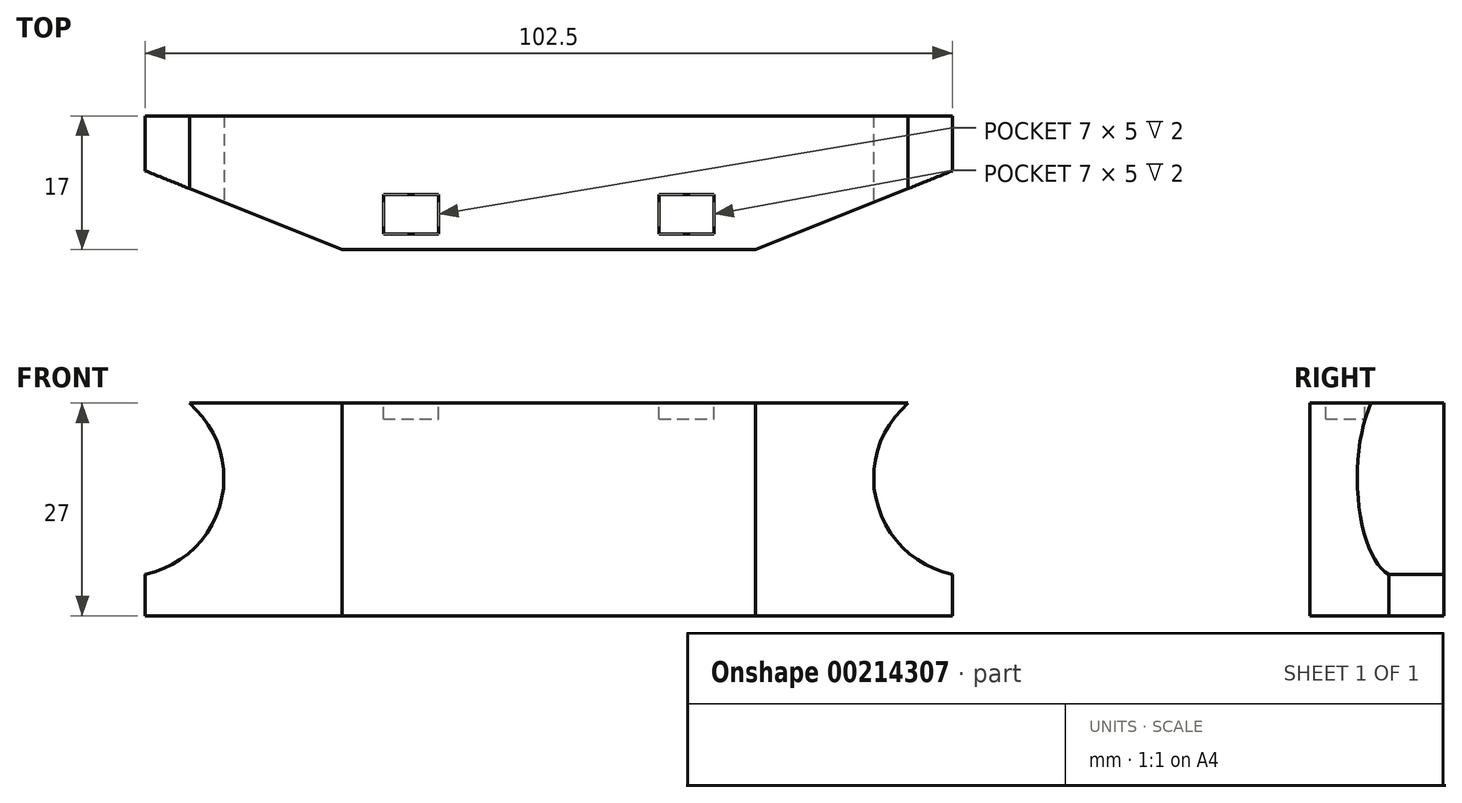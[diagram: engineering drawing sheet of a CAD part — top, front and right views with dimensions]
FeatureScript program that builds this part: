
annotation { "Feature Type Name" : "Feature", "Feature Type Description" : "" }
export const myFeature = defineFeature(function(context is Context, id is Id, definition is map)
    precondition{}
    {
        {
            var Q0;
            Q0=qCreatedBy(makeId("Front.planeOp"),FACE);
            var sketch = newSketch(context, id + "F0", { "sketchPlane" : qUnion([Q0])});
            skLineSegment(sketch, "E0.bottom", {"start": v(51.25, 13.5) * mm, "end": v(-51.25, 13.5) * mm});
            skLineSegment(sketch, "E0.top", {"start": v(51.25, -13.5) * mm, "end": v(-51.25, -13.5) * mm});
            skLineSegment(sketch, "E0.left", {"start": v(51.25, 13.5) * mm, "end": v(51.25, -13.5) * mm});
            skLineSegment(sketch, "E0.right", {"start": v(-51.25, 13.5) * mm, "end": v(-51.25, -13.5) * mm});
            skPoint(sketch, "E0.middle", {"position": v(0, 0) * mm});
            skSolve(sketch);
        }
        {
            var Q0;
            Q0 = qSketchRegion(id + "F0", true);
            extrude(context, id + "F1", {"entities" : qUnion([Q0]), "depth" : 17 * mm});
        }
        {
            var Q0;
            Q0=makeQuery(id+"F1.opExtrude","SWEPT_FACE",FACE,{"disambiguationData":[OSD([sQuery(id+"F0.wireOp",EDGE,"E0.top")])]});
            var sketch = newSketch(context, id + "F2", { "sketchPlane" : qUnion([Q0])});
            skLineSegment(sketch, "E1.bottom", {"start": v(-26.25, 17) * mm, "end": v(26.25, 17) * mm, "construction": true});
            skLineSegment(sketch, "E1.top", {"start": v(-26.25, 0) * mm, "end": v(26.25, 0) * mm, "construction": true});
            skLineSegment(sketch, "E1.left", {"start": v(-26.25, 17) * mm, "end": v(-26.25, 0) * mm, "construction": true});
            skLineSegment(sketch, "E1.right", {"start": v(26.25, 17) * mm, "end": v(26.25, 0) * mm, "construction": true});
            skLineSegment(sketch, "E2", {"start": v(-26.25, 17) * mm, "end": v(-51.25, 7) * mm});
            skLineSegment(sketch, "E3", {"start": v(-51.25, 7) * mm, "end": v(-51.25, 17) * mm});
            skLineSegment(sketch, "E4", {"start": v(-51.25, 17) * mm, "end": v(-26.25, 17) * mm});
            skLineSegment(sketch, "E5", {"start": v(26.25, 17) * mm, "end": v(51.25, 7) * mm});
            skLineSegment(sketch, "E6", {"start": v(51.25, 7) * mm, "end": v(51.25, 17) * mm});
            skLineSegment(sketch, "E7", {"start": v(51.25, 17) * mm, "end": v(26.25, 17) * mm});
            skSolve(sketch);
        }
        {
            var Q0;
            Q0 = qSketchRegion(id + "F2", true);
            extrude(context, id + "F3", {"entities" : qUnion([Q0]), "operationType" : NewBodyOperationType.REMOVE, "oppositeDirection" : true, "depth" : 190 * mm});
        }
        {
            var Q0;
            Q0=makeQuery(id+"F1.opExtrude","CAP_FACE",FACE,{"disambiguationData":[OSD([sQuery(id+"F0.wireOp",EDGE,"E0.bottom"),sQuery(id+"F0.wireOp",EDGE,"E0.top"),sQuery(id+"F0.wireOp",EDGE,"E0.left"),sQuery(id+"F0.wireOp",EDGE,"E0.right")])],"isStart":false});
            var sketch = newSketch(context, id + "F4", { "sketchPlane" : qUnion([Q0])});
            skLineSegment(sketch, "E8", {"start": v(0, -13.5) * mm, "end": v(0, 4) * mm, "construction": true});
            skPoint(sketch, "E8.endSnap0", {"position": v(0, -13.5) * mm});
            skLineSegment(sketch, "E9.bottom", {"start": v(53.75, 4) * mm, "end": v(-53.75, 4) * mm, "construction": true});
            skLineSegment(sketch, "E9.top", {"start": v(53.75, 4) * mm, "end": v(-53.75, 4) * mm, "construction": true});
            skLineSegment(sketch, "E9.left", {"start": v(53.75, 4) * mm, "end": v(53.75, 4) * mm});
            skLineSegment(sketch, "E9.right", {"start": v(-53.75, 4) * mm, "end": v(-53.75, 4) * mm});
            skPoint(sketch, "E9.middle", {"position": v(0, 4) * mm});
            skCircle(sketch, "E10", {"center": v(-53.75, 4) * mm, "radius": 12.5 * mm});
            skCircle(sketch, "E11", {"center": v(53.75, 4) * mm, "radius": 12.5 * mm});
            skSolve(sketch);
        }
        {
            var Q0;
            Q0 = qSketchRegion(id + "F4", true);
            extrude(context, id + "F5", {"entities" : qUnion([Q0]), "operationType" : NewBodyOperationType.REMOVE, "oppositeDirection" : true, "depth" : 25 * mm});
        }
        {
            var Q0;
            Q0=makeQuery(id+"F1.opExtrude","SWEPT_FACE",FACE,{"disambiguationData":[OSD([sQuery(id+"F0.wireOp",EDGE,"E0.bottom")])]});
            var sketch = newSketch(context, id + "F6", { "sketchPlane" : qUnion([Q0])});
            skLineSegment(sketch, "E12.bottom", {"start": v(-17.5, -12.5) * mm, "end": v(17.5, -12.5) * mm, "construction": true});
            skLineSegment(sketch, "E12.top", {"start": v(-17.5, -14.55) * mm, "end": v(17.5, -14.55) * mm, "construction": true});
            skLineSegment(sketch, "E12.left", {"start": v(-17.5, -14.55) * mm, "end": v(-17.5, -12.5) * mm, "construction": true});
            skLineSegment(sketch, "E12.right", {"start": v(17.5, -14.55) * mm, "end": v(17.5, -12.5) * mm, "construction": true});
            skPoint(sketch, "E12.middle", {"position": v(0, -13.53) * mm});
            skLineSegment(sketch, "E13.bottom", {"start": v(14, -15) * mm, "end": v(21, -15) * mm});
            skLineSegment(sketch, "E13.top", {"start": v(14, -10) * mm, "end": v(21, -10) * mm});
            skLineSegment(sketch, "E13.left", {"start": v(14, -15) * mm, "end": v(14, -10) * mm});
            skLineSegment(sketch, "E13.right", {"start": v(21, -15) * mm, "end": v(21, -10) * mm});
            skPoint(sketch, "E13.middle", {"position": v(17.5, -12.5) * mm});
            skLineSegment(sketch, "E14.bottom", {"start": v(-21, -15) * mm, "end": v(-14, -15) * mm});
            skLineSegment(sketch, "E14.top", {"start": v(-21, -10) * mm, "end": v(-14, -10) * mm});
            skLineSegment(sketch, "E14.left", {"start": v(-21, -15) * mm, "end": v(-21, -10) * mm});
            skLineSegment(sketch, "E14.right", {"start": v(-14, -15) * mm, "end": v(-14, -10) * mm});
            skPoint(sketch, "E14.middle", {"position": v(-17.5, -12.5) * mm});
            skSolve(sketch);
        }
        {
            var Q0;
            Q0 = qSketchRegion(id + "F6", true);
            extrude(context, id + "F7", {"entities" : qUnion([Q0]), "operationType" : NewBodyOperationType.REMOVE, "oppositeDirection" : true, "depth" : 2 * mm});
        }
    });
